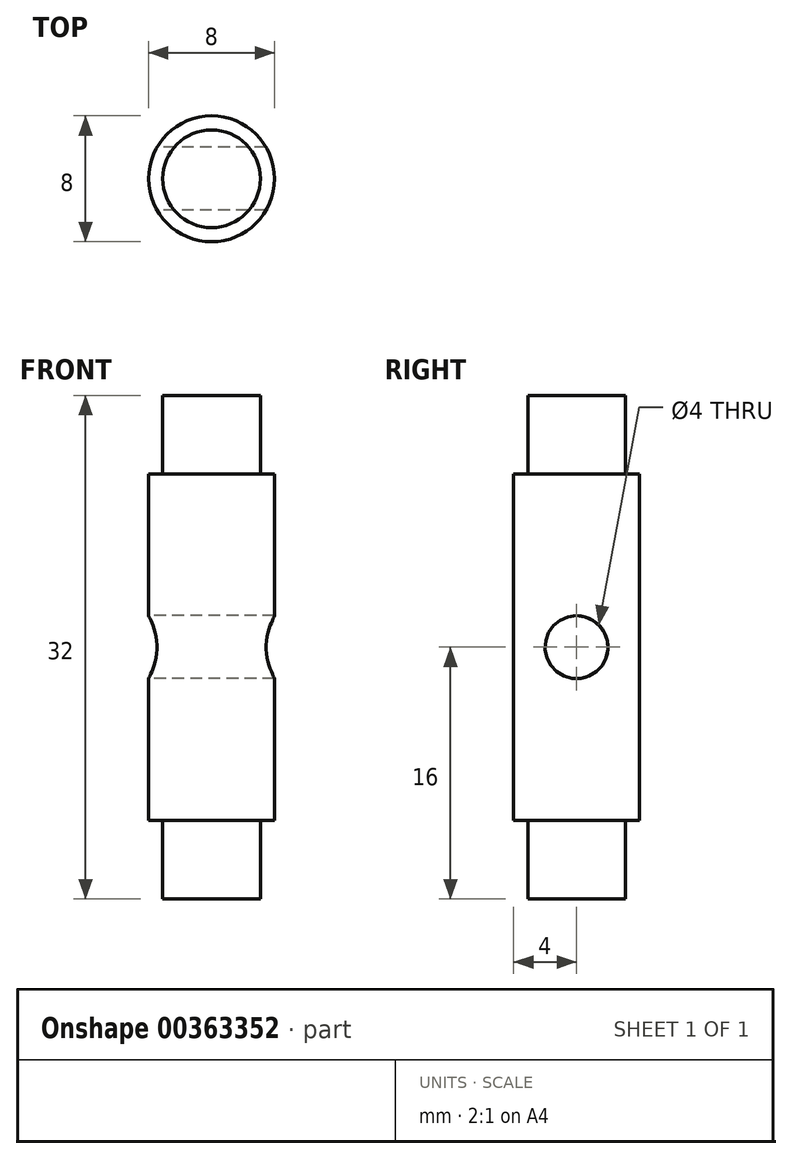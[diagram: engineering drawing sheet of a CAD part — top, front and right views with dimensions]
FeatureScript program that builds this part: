
annotation { "Feature Type Name" : "Feature", "Feature Type Description" : "" }
export const myFeature = defineFeature(function(context is Context, id is Id, definition is map)
    precondition{}
    {
        {
            var Q0;
            Q0=qCreatedBy(makeId("Top.planeOp"),FACE);
            var sketch = newSketch(context, id + "F0", { "sketchPlane" : qUnion([Q0])});
            skCircle(sketch, "E0", {"center": v(0, 0) * mm, "radius": 4 * mm});
            skCircle(sketch, "E1", {"center": v(0, 0) * mm, "radius": 3.1 * mm});
            skSolve(sketch);
        }
        {
            var Q0;
            Q0=makeQuery(id+"F0.imprint","IMPRINT",FACE,{"disambiguationData":[TD([[makeQuery(id+"F0.imprint","IMPRINT",EDGE,{"derivedFrom":sQuery(id+"F0.wireOp",EDGE,"E0")}),1.0]])]});
            extrude(context, id + "F1", {"entities" : qUnion([Q0]), "depth" : 22 * mm});
        }
        {
            var Q0;
            Q0=makeQuery(id+"F0.imprint","IMPRINT",FACE,{"disambiguationData":[TD([[makeQuery(id+"F0.imprint","IMPRINT",EDGE,{"derivedFrom":sQuery(id+"F0.wireOp",EDGE,"E1")}),1.0]])]});
            extrude(context, id + "F2", {"entities" : qUnion([Q0]), "operationType" : NewBodyOperationType.ADD, "depth" : 27 * mm});
        }
        {
            var Q0;
            Q0=makeQuery(id+"F0.imprint","IMPRINT",FACE,{"disambiguationData":[TD([[makeQuery(id+"F0.imprint","IMPRINT",EDGE,{"derivedFrom":sQuery(id+"F0.wireOp",EDGE,"E1")}),1.0]])]});
            extrude(context, id + "F3", {"entities" : qUnion([Q0]), "operationType" : NewBodyOperationType.ADD, "oppositeDirection" : true, "depth" : 5 * mm});
        }
        {
            var Q0;
            Q0=qCreatedBy(makeId("Right.planeOp"),FACE);
            var sketch = newSketch(context, id + "F4", { "sketchPlane" : qUnion([Q0])});
            skLineSegment(sketch, "E2", {"start": v(0, 0) * mm, "end": v(0, 45.02) * mm});
            skCircle(sketch, "E3", {"center": v(0, 11) * mm, "radius": 2 * mm});
            skSolve(sketch);
        }
        {
            var Q0;
            Q0 = qSketchRegion(id + "F4", true);
            extrude(context, id + "F5", {"entities" : qUnion([Q0]), "operationType" : NewBodyOperationType.REMOVE, "depth" : 25 * mm});
        }
        {
            var Q0;
            Q0=makeQuery(id+"F5.boolean.opBoolean","COPY",FACE,{"derivedFrom":makeQuery(id+"F5.opExtrude","CAP_FACE",FACE,{"disambiguationData":[OSD([sQuery(id+"F4.wireOp",EDGE,"E3")])],"isStart":true})});
            extrude(context, id + "F6", {"entities" : qUnion([Q0]), "operationType" : NewBodyOperationType.REMOVE, "oppositeDirection" : true, "depth" : 25 * mm});
        }
    });
